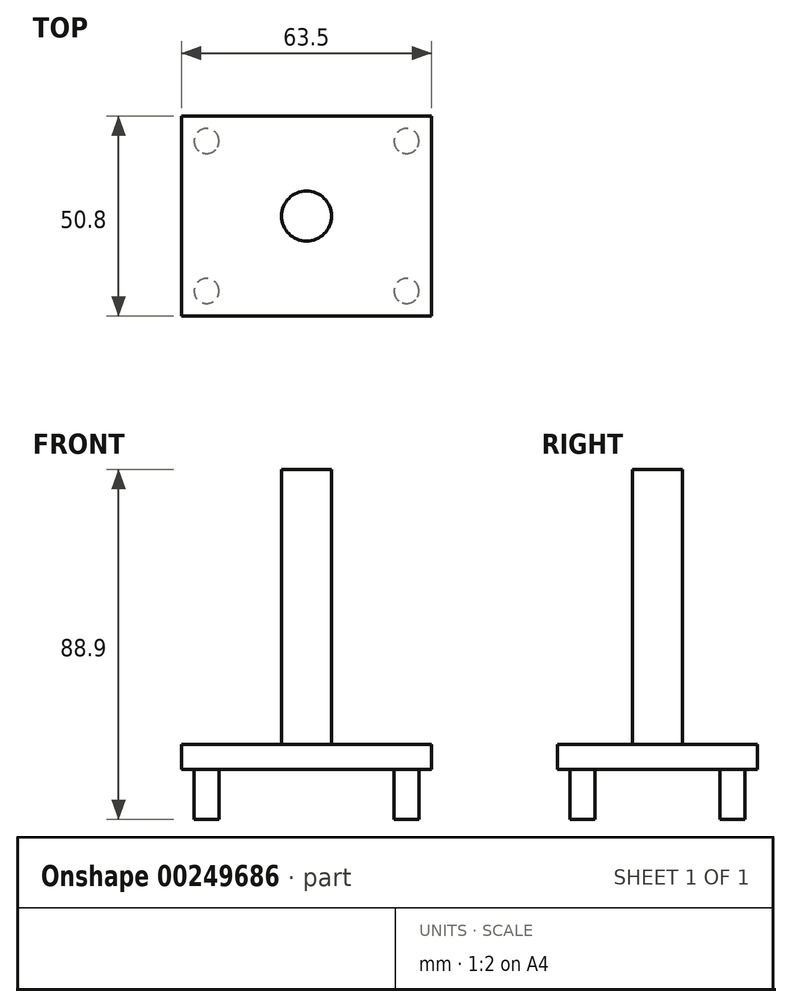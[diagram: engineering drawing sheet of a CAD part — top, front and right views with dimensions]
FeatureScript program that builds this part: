
annotation { "Feature Type Name" : "Feature", "Feature Type Description" : "" }
export const myFeature = defineFeature(function(context is Context, id is Id, definition is map)
    precondition{}
    {
        {
            var Q0;
            Q0=qCreatedBy(makeId("Top.planeOp"),FACE);
            var sketch = newSketch(context, id + "F0", { "sketchPlane" : qUnion([Q0])});
            skLineSegment(sketch, "E0.bottom", {"start": v(-31.75, -25.4) * mm, "end": v(31.75, -25.4) * mm});
            skLineSegment(sketch, "E0.top", {"start": v(-31.75, 25.4) * mm, "end": v(31.75, 25.4) * mm});
            skLineSegment(sketch, "E0.left", {"start": v(-31.75, -25.4) * mm, "end": v(-31.75, 25.4) * mm});
            skLineSegment(sketch, "E0.right", {"start": v(31.75, -25.4) * mm, "end": v(31.75, 25.4) * mm});
            skSolve(sketch);
        }
        {
            var Q0;
            Q0=makeQuery(id+"F0.imprint","IMPRINT",FACE,{"disambiguationData":[TD([[makeQuery(id+"F0.imprint","IMPRINT",EDGE,{"derivedFrom":sQuery(id+"F0.wireOp",EDGE,"E0.bottom")}),1.0]])]});
            extrude(context, id + "F1", {"entities" : qUnion([Q0]), "depth" : 6.35 * mm});
        }
        {
            var Q0;
            Q0=makeQuery(id+"F1.opExtrude","CAP_FACE",FACE,{"disambiguationData":[OSD([sQuery(id+"F0.wireOp",EDGE,"E0.bottom"),sQuery(id+"F0.wireOp",EDGE,"E0.top"),sQuery(id+"F0.wireOp",EDGE,"E0.left"),sQuery(id+"F0.wireOp",EDGE,"E0.right")])],"isStart":false});
            var sketch = newSketch(context, id + "F2", { "sketchPlane" : qUnion([Q0])});
            skCircle(sketch, "E1", {"center": v(0, 0) * mm, "radius": 6.35 * mm});
            skSolve(sketch);
        }
        {
            var Q0;
            Q0=makeQuery(id+"F2.imprint","IMPRINT",FACE,{"disambiguationData":[TD([[makeQuery(id+"F2.imprint","IMPRINT",EDGE,{"derivedFrom":sQuery(id+"F2.wireOp",EDGE,"E1")}),1.0]])]});
            extrude(context, id + "F3", {"entities" : qUnion([Q0]), "operationType" : NewBodyOperationType.ADD, "depth" : 69.85 * mm});
        }
        {
            var Q0;
            Q0=makeQuery(id+"F1.opExtrude","CAP_FACE",FACE,{"disambiguationData":[OSD([sQuery(id+"F0.wireOp",EDGE,"E0.bottom"),sQuery(id+"F0.wireOp",EDGE,"E0.top"),sQuery(id+"F0.wireOp",EDGE,"E0.left"),sQuery(id+"F0.wireOp",EDGE,"E0.right")])],"isStart":true});
            var sketch = newSketch(context, id + "F4", { "sketchPlane" : qUnion([Q0])});
            skCircle(sketch, "E2", {"center": v(-25.4, 19.05) * mm, "radius": 3.18 * mm});
            skCircle(sketch, "E3", {"center": v(25.4, 19.05) * mm, "radius": 3.18 * mm});
            skCircle(sketch, "E4", {"center": v(-25.4, -19.05) * mm, "radius": 3.18 * mm});
            skCircle(sketch, "E5", {"center": v(25.4, -19.05) * mm, "radius": 3.18 * mm});
            skSolve(sketch);
        }
        {
            var Q0;
            Q0 = qSketchRegion(id + "F4", true);
            extrude(context, id + "F5", {"entities" : qUnion([Q0]), "operationType" : NewBodyOperationType.ADD, "depth" : 12.7 * mm});
        }
    });
